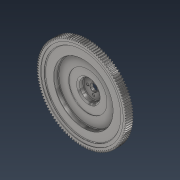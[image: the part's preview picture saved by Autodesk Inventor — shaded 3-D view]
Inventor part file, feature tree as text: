
AUTODESK INVENTOR PART (.ipt)
format: ipt  version: 2022 (Build 260153000, 153)  size: 1,881,600 bytes
history: native  units: mm
features: extrude x13, sketch x5, fillet x4, other x3, chamfer x3, hole x1, projected_geometry x1
ambient origin geometry x8: Origin, YZ Plane, XZ Plane, XY Plane, X Axis, Y Axis, Z Axis, Center Point
bodies: Solid1 (feature_tree)
feature tree (30):
  other  "Spur Gear1"
  extrude  "Extrusion1"  Depth=10.0mm
  sketch  "Sketch1"  dims[d0=10.0mm d1=280.0mm]
  extrude  "Extrusion2"  Depth=200.0mm
  extrude  "Extrusion3"  Depth=70.0mm
  extrude  "Extrusion4"  Depth=50.0mm TaperAngle=0.0deg
  extrude  "Extrusion5"  Depth=5.0mm TaperAngle=0.0deg
  extrude  "Extrusion6"  Depth=20.0mm TaperAngle=0.0deg
  extrude  "Extrusion7"  Depth=22.0mm TaperAngle=0.0deg
  hole  "Hole1"  [1 undecoded]
  chamfer  "Chamfer1"  Distance=40.0mm
  fillet  "Fillet1"  Radius=41.0mm
  chamfer  "Chamfer2"  Distance=40.0mm Angle=360.0deg
  extrude  "Extrusion8"  Depth=5.0mm TaperAngle=45.0deg
  sketch  "Sketch5"  dims[d9=2.0mm d10=0.0mm d11=5.0mm d12=0.0mm d13=20.0mm d14=0.0mm d15=22.0mm d16=0.0mm d17=0.0mm d18=0.0mm d19=40.0mm d20=0.0mm d21=41.0mm d22=40.0mm d24=360.0deg d26=8.0mm d27=12.4mm d28=4.0mm d29=2.0mm d30=90.0deg d31=12.4mm d32=20.594885mm d33=5.0mm d34=2.0mm d35=45.0deg d36=2.0mm d37=1.0mm d38=2.0mm d39=45.0deg d40=55.0mm d41=70.0mm d42=5.0mm d43=0.0mm d44=310.0mm d45=255.0mm d46=150.0mm d47=11.0mm d48=0.0mm d49=14.0mm d50=0.0mm d51=30.0mm d52=0.0mm d53=28.0mm d54=0.0mm d55=7.0mm d56=1.0mm d57=4.0mm d58=0.5mm d59=2.0mm d60=45.0deg d61=25.0mm d62=14.0mm d63=0.0mm]
  extrude  "Extrusion9"  Depth=2.0mm
  extrude  "Extrusion10"  Depth=1.0mm TaperAngle=45.0deg
  extrude  "Extrusion11"  Depth=55.0mm
  extrude  "Extrusion12"  Depth=14.0mm
  fillet  "Fillet2"  Radius=5.0mm
  fillet  "Fillet3"  Radius=310.0mm
  fillet  "Fillet4"  Radius=255.0mm
  extrude  "Extrusion13"  Depth=14.0mm
  chamfer  "Chamfer3"  Distance=11.0mm
  other  "Solid1::Spur Gear1"
  other  "TaggingFeature1"
  sketch  "Sketch2"  dims[d2=260.0mm d3=200.0mm]
  projected_geometry  "Projected Loop1"
  sketch  "Sketch3"  dims[d4=28.3mm d5=70.0mm]
  sketch  "Sketch4"  dims[d6=130.0mm d7=50.0mm d8=0.0mm]
note: 1 required parameter value undecoded (feature->parameter linkage not recoverable at this tier; creation-order binding heuristic only, values carry confidence <= 0.55)
